# Revit family: HL_RU_Roof drain_HL64FSafe-B-221103
name_source: partatom
category: Instalační zařizovací předměty
units: mm (PartAtom-declared; Revit-internal decimal feet)

## family parameters
Bod výpočtu místnosti = Ano
Kóta kulaté spojky = Použít průměr
Nadpis OmniClass = Deck Waste Water Drains
Ořezat dutým tvarem při načtení = Ne
Sdílené = Ne
Typ dílu = Normální
Vždy vertikální = Ano
Založené na pracovní rovině = Ne
Číslo OmniClass = 23.70.50.21.24.14

## types (2) — shared parameters
Popis = Кровельные воронки
Přípoj CW = Ne
Přípoj HW = Ne
Přípoj odpadních dílů = Ano
Přípoj ventilace = Ne
URL = http://www.hutterer-lechner.com
Výrobce = HL Hutterer & Lechner GmbH
ВЫСОТА МОНТАЖА = 150mm
МАТЕРИАЛ = PP
РЕШЁТКА = Laubfangkorb d 262 mm
zero-valued in all types: Výchozí výška

## per-type parameters (varying)
| type | EAN | Indexovaná poznámka | Komentáře k typům | Model | ВЕС | НОМИНАЛЬНЫЙ ДИАМЕТР | РАЗМЕР |
| HL_Кровельная воронка_HL64FSafe_1 | 9003076041008 | HL64FSafe_1 | HL64FSafe/1, Воронка для аварийного водостока с горизонтальным выпуском DN110 с корпусом из ПП, с возможностью регулировки толщины слоя воды | HL64FSafe_1 | 2,273 [kg] | 110 mm | DN110 |
| HL_Кровельная воронка_HL64FSafe_7 | 9003076040995 | HL64FSafe_7 | HL64FSafe/7, Воронка для аварийного водостока с горизонтальным выпуском DN75 с корпусом из ПП, с возможностью регулировки толщины слоя воды | HL64FSafe_7 | 2,163 [kg] | 75 mm | DN75 |

## geometry (parser evidence)
native form markers: Sweep x3
no freeform markers — native parametric forms only
